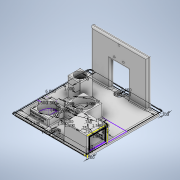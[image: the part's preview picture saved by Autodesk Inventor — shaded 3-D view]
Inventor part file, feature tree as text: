
AUTODESK INVENTOR PART (.ipt)
format: ipt  version: 2020 (Build 240168000, 168)  size: 1,792,512 bytes
history: native  units: in
note: dims shown in document units (in); Inventor stores cm internally (conversion verified against a paired STEP export)
features: extrude x15, sketch x9, fillet x7, hole x2
ambient origin geometry x8: Origin, YZ Plane, XZ Plane, XY Plane, X Axis, Y Axis, Z Axis, Center Point
bodies: Solid1 (feature_tree)
feature tree (33):
  sketch  "Sketch1"  dims[d0=5.6in d1=6.0in]
  extrude  "Extrusion1"  Depth=6.0in
  hole  "Hole1"  [1 undecoded]
  extrude  "Extrusion2"  Depth=5.6in
  extrude  "Extrusion3"  Depth=5.6in
  extrude  "Extrusion4"  Depth=0.25in TaperAngle=0.0deg
  extrude  "Extrusion5"  Depth=1.5in
  extrude  "Extrusion6"  Depth=1.5in
  hole  "Hole2"  [1 undecoded]
  extrude  "Extrusion7"  TaperAngle=180.0deg  [1 undecoded]
  extrude  "Extrusion8"  Depth=1.5in
  extrude  "Extrusion9"  Depth=1.5in
  sketch  "Sketch6"  dims[d11=0.266in d12=0.75in d13=0.625in d14=0.19in d15=0.5635in d16=1.0in d17=0.8108in d18=1.5in]
  extrude  "Extrusion10"  Depth=1.5in
  sketch  "Sketch7"  dims[d19=0.6in d20=1.5in]
  extrude  "Extrusion11"  Depth=1.5in
  extrude  "Extrusion12"  Depth=1.3in
  extrude  "Extrusion13"  Depth=1.3in
  fillet  "Fillet1"  Radius=0.5in
  fillet  "Fillet2"  Radius=0.5in
  fillet  "Fillet3"  Radius=1.0in
  fillet  "Fillet4"  Radius=1.5in
  fillet  "Fillet5"  Radius=0.325in
  fillet  "Fillet6"  Radius=2.0in
  fillet  "Fillet7"  Radius=1.5in
  sketch  "Sketch8"  dims[d21=1.5in d22=0.6in]
  sketch  "Sketch9"  dims[d23=1.5in d24=180.0deg d25=1.5in d26=1.5in d27=1.5in d28=1.5in d29=1.3in d30=1.3in d31=0.5in d32=0.0in d33=0.5in d34=0.0in d35=1.0in d36=0.0in d37=1.5in d38=0.325in d39=2.0in d40=0.0in d41=1.5in d42=0.0in d43=0.333in d44=0.96in d45=0.356in d46=0.356in d47=0.134in d48=0.75in d49=0.256in d50=0.118in d51=90.0deg d52=1.0in d53=0.8108in d54=1.75in d55=1.0in d56=1.0in d57=1.0in d58=0.78in d59=1.5in d60=0.0in d61=0.25in d62=0.25in d63=1.5in d64=0.0in d65=1.25in d66=0.0in d67=0.125in d68=0.125in d69=0.125in d70=0.125in d71=1.725in d72=0.0in d73=0.25in d74=0.25in d75=1.043in d76=0.748in d77=0.25in d78=0.0in d79=0.25in d80=0.25in d81=0.0625in d82=0.0625in d83=0.0625in d84=0.0625in d85=0.1875in d86=0.0in d87=0.125in d88=0.0in d89=0.125in d90=0.125in d91=0.0625in d92=0.0625in d93=0.0625in d94=0.0625in d95=0.0625in d96=0.0197in d97=0.0in d98=0.0197in d99=0.0in]
  extrude  "Extrusion14"  Depth=0.333in
  extrude  "Extrusion15"  Depth=0.96in
  sketch  "Sketch2"  dims[d2=0.5in d3=90.0deg]
  sketch  "Sketch3"  dims[d4=0.5in d5=5.6in]
  sketch  "Sketch4"  dims[d6=0.2in d7=5.6in]
  sketch  "Sketch5"  dims[d8=0.2in d9=0.25in d10=0.0in]
note: 3 required parameter values undecoded (feature->parameter linkage not recoverable at this tier; creation-order binding heuristic only, values carry confidence <= 0.55)
